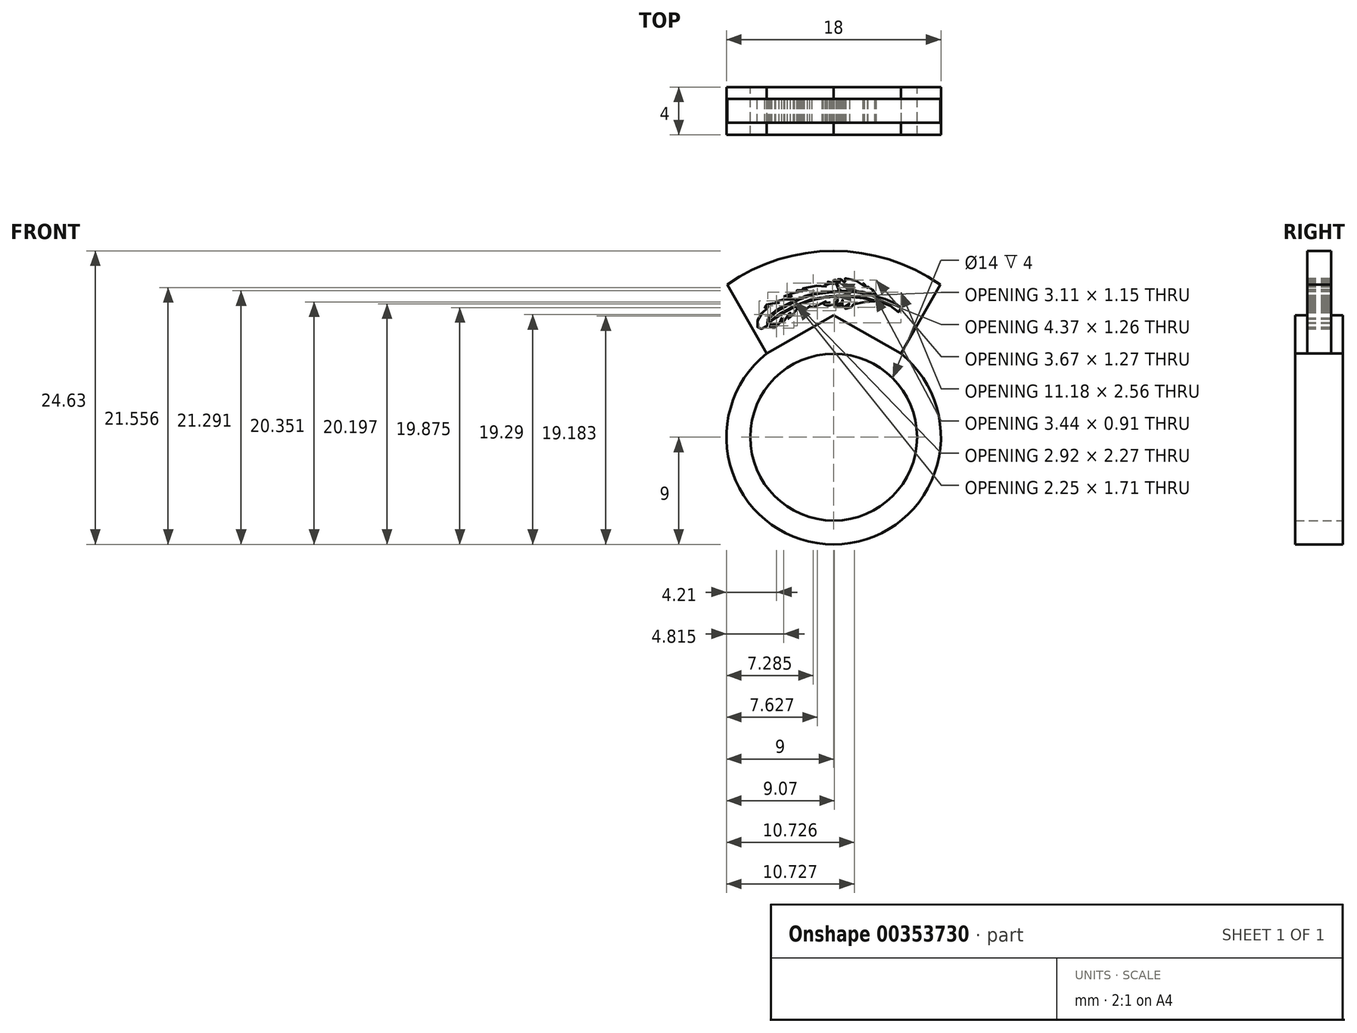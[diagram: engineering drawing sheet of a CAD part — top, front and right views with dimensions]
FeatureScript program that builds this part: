
annotation { "Feature Type Name" : "Feature", "Feature Type Description" : "" }
export const myFeature = defineFeature(function(context is Context, id is Id, definition is map)
    precondition{}
    {
        {
            var Q0;
            Q0=qCreatedBy(makeId("Front.planeOp"),FACE);
            var sketch = newSketch(context, id + "F0", { "sketchPlane" : qUnion([Q0])});
            skCircle(sketch, "E0", {"center": v(0, 0) * mm, "radius": 7 * mm});
            skCircle(sketch, "E1", {"center": v(0, 0) * mm, "radius": 9 * mm});
            skSolve(sketch);
        }
        {
            var Q0;
            Q0 = qSketchRegion(id + "F0", true);
            extrude(context, id + "F1", {"entities" : qUnion([Q0]), "depth" : 4 * mm});
        }
        {
            var Q0;
            Q0=makeQuery(id+"F1.opExtrude","CAP_FACE",FACE,{"disambiguationData":[OSD([sQuery(id+"F0.wireOp",EDGE,"E0"),sQuery(id+"F0.wireOp",EDGE,"E1")])],"isStart":false});
            var sketch = newSketch(context, id + "F2", { "sketchPlane" : qUnion([Q0])});
            skLineSegment(sketch, "E2", {"start": v(-5.64, 7.02) * mm, "end": v(-8.94, 12.8) * mm});
            skLineSegment(sketch, "E3", {"start": v(5.64, 7.02) * mm, "end": v(8.94, 12.8) * mm});
            skArc(sketch, "E4", {"start": v(8.94, 12.8) * mm, "mid": v(0, 15.63) * mm, "end": v(-8.94, 12.8) * mm});
            skSolve(sketch);
        }
        {
            var Q0;
            {var subQ0=sQuery(id+"F2.wireOp",EDGE,"E2");Q0=makeQuery(id+"F2.imprint","IMPRINT",FACE,{"disambiguationData":[TD([[makeQuery(id+"F2.imprint","IMPRINT",EDGE,{"derivedFrom":subQ0}),-1.0]])]});}
            extrude(context, id + "F3", {"entities" : qUnion([Q0]), "operationType" : NewBodyOperationType.ADD, "oppositeDirection" : true, "depth" : 4 * mm});
        }
        {
            var Q0;
            Q0=makeQuery(id+"F3.opExtrude","SWEPT_FACE",FACE,{"disambiguationData":[OSD([sQuery(id+"F2.wireOp",EDGE,"E2")])]});
            var sketch = newSketch(context, id + "F4", { "sketchPlane" : qUnion([Q0])});
            skLineSegment(sketch, "E5", {"start": v(1, 15.54) * mm, "end": v(1, 8.89) * mm});
            skLineSegment(sketch, "E6", {"start": v(1, 8.89) * mm, "end": v(3, 8.89) * mm});
            skLineSegment(sketch, "E7", {"start": v(3, 8.89) * mm, "end": v(3, 15.54) * mm});
            skLineSegment(sketch, "E8", {"start": v(3, 15.54) * mm, "end": v(1, 15.54) * mm});
            skSolve(sketch);
        }
        {
            var Q0;
            {var subQ0=sQuery(id+"F4.wireOp",EDGE,"E7");Q0=makeQuery(id+"F4.imprint","IMPRINT",FACE,{"disambiguationData":[TD([[makeQuery(id+"F4.imprint","IMPRINT",EDGE,{"derivedFrom":subQ0}),-1.0]])]});}
            var Q1;
            {var subQ0=sQuery(id+"F4.wireOp",EDGE,"E5");Q1=makeQuery(id+"F4.imprint","IMPRINT",FACE,{"disambiguationData":[TD([[makeQuery(id+"F4.imprint","IMPRINT",EDGE,{"derivedFrom":subQ0}),-1.0]])]});}
            extrude(context, id + "F5", {"entities" : qUnion([Q0, Q1]), "operationType" : NewBodyOperationType.REMOVE, "endBound" : BoundingType.THROUGH_ALL, "oppositeDirection" : true, "depth" : 25 * mm});
        }
        {
            var Q0;
            Q0=makeQuery(id+"F3.opExtrude","SWEPT_FACE",FACE,{"disambiguationData":[OSD([sQuery(id+"F2.wireOp",EDGE,"E3")])]});
            var sketch = newSketch(context, id + "F6", { "sketchPlane" : qUnion([Q0])});
            skLineSegment(sketch, "E9", {"start": v(-3, 15.54) * mm, "end": v(-3, 8.89) * mm});
            skLineSegment(sketch, "E10", {"start": v(-3, 8.89) * mm, "end": v(-1, 8.89) * mm});
            skLineSegment(sketch, "E11", {"start": v(-1, 8.89) * mm, "end": v(-1, 15.54) * mm});
            skLineSegment(sketch, "E12", {"start": v(-1, 15.54) * mm, "end": v(-3, 15.54) * mm});
            skSolve(sketch);
        }
        {
            var Q0;
            {var subQ0=sQuery(id+"F6.wireOp",EDGE,"E9");Q0=makeQuery(id+"F6.imprint","IMPRINT",FACE,{"disambiguationData":[TD([[makeQuery(id+"F6.imprint","IMPRINT",EDGE,{"derivedFrom":subQ0}),-1.0]])]});}
            var Q1;
            {var subQ0=sQuery(id+"F6.wireOp",EDGE,"E11");Q1=makeQuery(id+"F6.imprint","IMPRINT",FACE,{"disambiguationData":[TD([[makeQuery(id+"F6.imprint","IMPRINT",EDGE,{"derivedFrom":subQ0}),-1.0]])]});}
            extrude(context, id + "F7", {"entities" : qUnion([Q0, Q1]), "operationType" : NewBodyOperationType.REMOVE, "endBound" : BoundingType.THROUGH_ALL, "oppositeDirection" : true, "depth" : 25 * mm});
        }
        {
            var Q0;
            {var subQ0=sQuery(id+"F2.wireOp",EDGE,"E2");var subQ1=sQuery(id+"F2.wireOp",EDGE,"E4");var subQ2=makeQuery(id+"F3.opExtrude","SWEPT_EDGE",EDGE,{"disambiguationData":[OSD([subQ0,subQ1])]});Q0=makeQuery(id+"F5.boolean.opBoolean","COPY",FACE,{"derivedFrom":makeQuery(id+"F5.opExtrude","SWEPT_FACE",FACE,{"disambiguationData":[OSD([subQ0,subQ1]),TDD([makeQuery(id+"F4.imprint","IMPRINT",EDGE,{"disambiguationData":[TD([[makeQuery(id+"F4.imprint","INTERSECT",VERTEX,{"derivedFrom":[subQ2,makeQuery(id+"F3.opExtrude","CAP_EDGE",EDGE,{"disambiguationData":[OSD([subQ0])],"isStart":false})]}),-1.0]])],"derivedFrom":subQ2})])]})});}
            extrude(context, id + "F8", {"entities" : qUnion([Q0]), "operationType" : NewBodyOperationType.REMOVE, "endBound" : BoundingType.THROUGH_ALL, "oppositeDirection" : true, "depth" : 25 * mm});
        }
        {
            var Q0;
            {var subQ0=sQuery(id+"F2.wireOp",EDGE,"E2");var subQ1=sQuery(id+"F2.wireOp",EDGE,"E4");var subQ2=makeQuery(id+"F3.opExtrude","SWEPT_EDGE",EDGE,{"disambiguationData":[OSD([subQ0,subQ1])]});Q0=makeQuery(id+"F5.boolean.opBoolean","COPY",FACE,{"derivedFrom":makeQuery(id+"F5.opExtrude","SWEPT_FACE",FACE,{"disambiguationData":[OSD([subQ0,subQ1]),TDD([makeQuery(id+"F4.imprint","IMPRINT",EDGE,{"disambiguationData":[TD([[makeQuery(id+"F4.imprint","INTERSECT",VERTEX,{"derivedFrom":[subQ2,makeQuery(id+"F3.opExtrude","CAP_EDGE",EDGE,{"disambiguationData":[OSD([subQ0])],"isStart":true})]}),1.0]])],"derivedFrom":subQ2})])]})});}
            extrude(context, id + "F9", {"entities" : qUnion([Q0]), "operationType" : NewBodyOperationType.REMOVE, "endBound" : BoundingType.THROUGH_ALL, "oppositeDirection" : true, "depth" : 25 * mm});
        }
        {
            var Q0;
            {var subQ0=sQuery(id+"F2.wireOp",EDGE,"E3");var subQ1=sQuery(id+"F2.wireOp",EDGE,"E4");var subQ2=makeQuery(id+"F3.opExtrude","SWEPT_EDGE",EDGE,{"disambiguationData":[OSD([subQ0,subQ1])]});Q0=makeQuery(id+"F7.boolean.opBoolean","COPY",FACE,{"derivedFrom":makeQuery(id+"F7.opExtrude","SWEPT_FACE",FACE,{"disambiguationData":[OSD([subQ0,subQ1]),TDD([makeQuery(id+"F6.imprint","IMPRINT",EDGE,{"disambiguationData":[TD([[makeQuery(id+"F6.imprint","INTERSECT",VERTEX,{"derivedFrom":[subQ2,makeQuery(id+"F3.opExtrude","CAP_EDGE",EDGE,{"disambiguationData":[OSD([subQ0])],"isStart":true})]}),1.0]])],"derivedFrom":subQ2})])]})});}
            var Q1;
            {var subQ0=sQuery(id+"F2.wireOp",EDGE,"E3");var subQ1=sQuery(id+"F2.wireOp",EDGE,"E4");var subQ2=makeQuery(id+"F3.opExtrude","SWEPT_EDGE",EDGE,{"disambiguationData":[OSD([subQ0,subQ1])]});Q1=makeQuery(id+"F7.boolean.opBoolean","COPY",FACE,{"derivedFrom":makeQuery(id+"F7.opExtrude","SWEPT_FACE",FACE,{"disambiguationData":[OSD([subQ0,subQ1]),TDD([makeQuery(id+"F6.imprint","IMPRINT",EDGE,{"disambiguationData":[TD([[makeQuery(id+"F6.imprint","INTERSECT",VERTEX,{"derivedFrom":[subQ2,makeQuery(id+"F3.opExtrude","CAP_EDGE",EDGE,{"disambiguationData":[OSD([subQ0])],"isStart":false})]}),-1.0]])],"derivedFrom":subQ2})])]})});}
            extrude(context, id + "F10", {"entities" : qUnion([Q0, Q1]), "operationType" : NewBodyOperationType.REMOVE, "endBound" : BoundingType.THROUGH_ALL, "oppositeDirection" : true, "depth" : 25 * mm});
        }
        {
            var Q0;
            {var subQ0=sQuery(id+"F6.wireOp",EDGE,"E11");var subQ1=sQuery(id+"F2.wireOp",EDGE,"E4");var subQ2=sQuery(id+"F4.wireOp",EDGE,"E5");Q0=makeQuery(id+"F10.boolean.opBoolean","MERGE",FACE,{"derivedFrom":[makeQuery(id+"F8.boolean.opBoolean","MERGE",FACE,{"derivedFrom":[makeQuery(id+"F7.boolean.opBoolean","MERGE",FACE,{"derivedFrom":[makeQuery(id+"F5.boolean.opBoolean","COPY",FACE,{"derivedFrom":makeQuery(id+"F5.opExtrude","SWEPT_FACE",FACE,{"disambiguationData":[OSD([subQ2])]})}),makeQuery(id+"F7.opExtrude","SWEPT_FACE",FACE,{"disambiguationData":[OSD([subQ0])]})]}),makeQuery(id+"F8.opExtrude","SWEPT_FACE",FACE,{"disambiguationData":[OSD([sQuery(id+"F2.wireOp",EDGE,"E2"),subQ1,subQ2,sQuery(id+"F4.wireOp",EDGE,"E8")])]})]}),makeQuery(id+"F10.opExtrude","SWEPT_FACE",FACE,{"disambiguationData":[OSD([sQuery(id+"F2.wireOp",EDGE,"E3"),subQ1,subQ0,sQuery(id+"F6.wireOp",EDGE,"E12")])]})]});}
            var sketch = newSketch(context, id + "F11", { "sketchPlane" : qUnion([Q0])});
            skFitSpline(sketch, "E13", {"points": [v(-5.66, 10.87) * mm, v(-5.57, 10.45) * mm, v(-5.18, 10.74) * mm, v(-4.16, 11.27) * mm, v(-2.41, 11.75) * mm, v(-0.52, 11.88) * mm, v(0, 11.85) * mm, v(1.4, 11.68) * mm, v(3.3, 11) * mm, v(5.28, 9.8) * mm, v(5.51, 9.57) * mm, v(5.41, 9.99) * mm, v(4.45, 10.75) * mm, v(3.34, 11.32) * mm, v(1.84, 11.93) * mm, v(0, 12.17) * mm, v(-1.23, 12.22) * mm, v(-2.88, 12) * mm, v(-4.84, 11.4) * mm, v(-5.38, 11.12) * mm, v(-5.66, 10.87) * mm]});
            skSolve(sketch);
        }
        {
            var Q0;
            Q0 = qSketchRegion(id + "F11", true);
            extrude(context, id + "F12", {"entities" : qUnion([Q0]), "operationType" : NewBodyOperationType.REMOVE, "endBound" : BoundingType.THROUGH_ALL, "oppositeDirection" : true, "depth" : 25 * mm});
        }
        {
            var Q0;
            {var subQ0=sQuery(id+"F6.wireOp",EDGE,"E11");var subQ1=sQuery(id+"F2.wireOp",EDGE,"E4");var subQ2=sQuery(id+"F4.wireOp",EDGE,"E5");Q0=makeQuery(id+"F10.boolean.opBoolean","MERGE",FACE,{"derivedFrom":[makeQuery(id+"F8.boolean.opBoolean","MERGE",FACE,{"derivedFrom":[makeQuery(id+"F7.boolean.opBoolean","MERGE",FACE,{"derivedFrom":[makeQuery(id+"F5.boolean.opBoolean","COPY",FACE,{"derivedFrom":makeQuery(id+"F5.opExtrude","SWEPT_FACE",FACE,{"disambiguationData":[OSD([subQ2])]})}),makeQuery(id+"F7.opExtrude","SWEPT_FACE",FACE,{"disambiguationData":[OSD([subQ0])]})]}),makeQuery(id+"F8.opExtrude","SWEPT_FACE",FACE,{"disambiguationData":[OSD([sQuery(id+"F2.wireOp",EDGE,"E2"),subQ1,subQ2,sQuery(id+"F4.wireOp",EDGE,"E8")])]})]}),makeQuery(id+"F10.opExtrude","SWEPT_FACE",FACE,{"disambiguationData":[OSD([sQuery(id+"F2.wireOp",EDGE,"E3"),subQ1,subQ0,sQuery(id+"F6.wireOp",EDGE,"E12")])]})]});}
            var sketch = newSketch(context, id + "F13", { "sketchPlane" : qUnion([Q0])});
            skFitSpline(sketch, "E14", {"points": [v(-3.45, 11.42) * mm, v(-3.13, 11.52) * mm, v(-2.56, 11.65) * mm, v(-1.78, 11.74) * mm, v(-0.99, 11.78) * mm, v(-0.56, 11.8) * mm, v(-0.22, 11.77) * mm, v(-0.31, 11.58) * mm, v(-0.26, 11.2) * mm, v(0, 10.91) * mm, v(-0.19, 10.94) * mm, v(-0.51, 11.24) * mm, v(-0.4, 11.02) * mm, v(-0.28, 10.9) * mm, v(-0.43, 10.93) * mm, v(-0.57, 11.08) * mm, v(-0.7, 11.33) * mm, v(-0.75, 11.52) * mm, v(-0.78, 11.17) * mm, v(-0.65, 10.91) * mm, v(-1.1, 11.03) * mm, v(-1.35, 11.24) * mm, v(-1.28, 11.06) * mm, v(-0.95, 10.78) * mm, v(-1.27, 10.85) * mm, v(-1.58, 11) * mm, v(-1.73, 11.18) * mm, v(-3.45, 11.42) * mm]});
            skFitSpline(sketch, "E15", {"points": [v(-3.56, 11.92) * mm, v(-2.94, 12.08) * mm, v(-2.33, 12.2) * mm, v(-1.6, 12.27) * mm, v(-0.95, 12.3) * mm, v(-0.5, 12.3) * mm, v(-0.35, 12.58) * mm, v(-0.32, 12.88) * mm, v(-0.14, 13.12) * mm, v(0.14, 13.18) * mm, v(-0.17, 13.2) * mm, v(-0.39, 13.04) * mm, v(-0.48, 12.86) * mm, v(-0.54, 13) * mm, v(-0.5, 13.16) * mm, v(-0.32, 13.28) * mm, v(-0.64, 13.24) * mm, v(-0.86, 13.08) * mm, v(-0.93, 12.96) * mm, v(-1.03, 13.08) * mm, v(-0.82, 13.3) * mm, v(-1.92, 13.11) * mm, v(-2.6, 12.69) * mm, v(-2.48, 12.9) * mm, v(-2.77, 12.65) * mm, v(-2.89, 12.42) * mm, v(-2.88, 12.69) * mm, v(-3.5, 12.05) * mm, v(-3.56, 11.92) * mm]});
            skSolve(sketch);
        }
        {
            var Q0;
            Q0=makeQuery(id+"F13.imprint","IMPRINT",FACE,{"disambiguationData":[TD([[makeQuery(id+"F13.imprint","IMPRINT",EDGE,{"derivedFrom":sQuery(id+"F13.wireOp",EDGE,"E14")}),-1.0]])]});
            var Q1;
            Q1=makeQuery(id+"F13.imprint","IMPRINT",FACE,{"disambiguationData":[TD([[makeQuery(id+"F13.imprint","IMPRINT",EDGE,{"derivedFrom":sQuery(id+"F13.wireOp",EDGE,"c0ec5056-5226-495e-9444-eb4ab02b29c7")}),1.0]])]});
            extrude(context, id + "F14", {"entities" : qUnion([Q0, Q1]), "operationType" : NewBodyOperationType.REMOVE, "endBound" : BoundingType.THROUGH_ALL, "oppositeDirection" : true, "depth" : 25 * mm});
        }
        {
            var Q0;
            {var subQ0=sQuery(id+"F6.wireOp",EDGE,"E11");var subQ1=sQuery(id+"F2.wireOp",EDGE,"E4");var subQ2=sQuery(id+"F4.wireOp",EDGE,"E5");Q0=makeQuery(id+"F10.boolean.opBoolean","MERGE",FACE,{"derivedFrom":[makeQuery(id+"F8.boolean.opBoolean","MERGE",FACE,{"derivedFrom":[makeQuery(id+"F7.boolean.opBoolean","MERGE",FACE,{"derivedFrom":[makeQuery(id+"F5.boolean.opBoolean","COPY",FACE,{"derivedFrom":makeQuery(id+"F5.opExtrude","SWEPT_FACE",FACE,{"disambiguationData":[OSD([subQ2])]})}),makeQuery(id+"F7.opExtrude","SWEPT_FACE",FACE,{"disambiguationData":[OSD([subQ0])]})]}),makeQuery(id+"F8.opExtrude","SWEPT_FACE",FACE,{"disambiguationData":[OSD([sQuery(id+"F2.wireOp",EDGE,"E2"),subQ1,subQ2,sQuery(id+"F4.wireOp",EDGE,"E8")])]})]}),makeQuery(id+"F10.opExtrude","SWEPT_FACE",FACE,{"disambiguationData":[OSD([sQuery(id+"F2.wireOp",EDGE,"E3"),subQ1,subQ0,sQuery(id+"F6.wireOp",EDGE,"E12")])]})]});}
            var sketch = newSketch(context, id + "F15", { "sketchPlane" : qUnion([Q0])});
            skSolve(sketch);
        }
        {
            var Q0;
            Q0 = qSketchRegion(id + "F13", true);
            var Q1;
            Q1=makeQuery(id+"F15.imprint","IMPRINT",FACE,{"disambiguationData":[TD([[makeQuery(id+"F15.imprint","IMPRINT",EDGE,{"derivedFrom":makeQuery(id+"F14.boolean.opBoolean","COPY",EDGE,{"derivedFrom":makeQuery(id+"F14.opExtrude","CAP_EDGE",EDGE,{"disambiguationData":[OSD([sQuery(id+"F13.wireOp",EDGE,"E14")])],"isStart":true})})}),-1.0]])]});
            extrude(context, id + "F16", {"entities" : qUnion([Q0, Q1]), "operationType" : NewBodyOperationType.REMOVE, "endBound" : BoundingType.THROUGH_ALL, "oppositeDirection" : true, "depth" : 25 * mm});
        }
        {
            var Q0;
            {var subQ0=sQuery(id+"F6.wireOp",EDGE,"E11");var subQ1=sQuery(id+"F2.wireOp",EDGE,"E4");var subQ2=sQuery(id+"F4.wireOp",EDGE,"E5");Q0=makeQuery(id+"F10.boolean.opBoolean","MERGE",FACE,{"derivedFrom":[makeQuery(id+"F8.boolean.opBoolean","MERGE",FACE,{"derivedFrom":[makeQuery(id+"F7.boolean.opBoolean","MERGE",FACE,{"derivedFrom":[makeQuery(id+"F5.boolean.opBoolean","COPY",FACE,{"derivedFrom":makeQuery(id+"F5.opExtrude","SWEPT_FACE",FACE,{"disambiguationData":[OSD([subQ2])]})}),makeQuery(id+"F7.opExtrude","SWEPT_FACE",FACE,{"disambiguationData":[OSD([subQ0])]})]}),makeQuery(id+"F8.opExtrude","SWEPT_FACE",FACE,{"disambiguationData":[OSD([sQuery(id+"F2.wireOp",EDGE,"E2"),subQ1,subQ2,sQuery(id+"F4.wireOp",EDGE,"E8")])]})]}),makeQuery(id+"F10.opExtrude","SWEPT_FACE",FACE,{"disambiguationData":[OSD([sQuery(id+"F2.wireOp",EDGE,"E3"),subQ1,subQ0,sQuery(id+"F6.wireOp",EDGE,"E12")])]})]});}
            var sketch = newSketch(context, id + "F17", { "sketchPlane" : qUnion([Q0])});
            skFitSpline(sketch, "E16", {"points": [v(-0.47, 12.28) * mm, v(-0.22, 12.27) * mm, v(-0.04, 12.26) * mm, v(0.27, 12.23) * mm, v(0.71, 12.2) * mm, v(1.2, 12.13) * mm, v(1.55, 12.07) * mm, v(2.1, 11.95) * mm, v(2.6, 11.77) * mm, v(3.2, 11.46) * mm, v(3.36, 11.55) * mm, v(3.73, 11.66) * mm, v(4.1, 11.61) * mm, v(3.87, 11.73) * mm, v(3.64, 11.77) * mm, v(3.37, 11.76) * mm, v(3.6, 11.86) * mm, v(3.83, 11.87) * mm, v(4.17, 11.81) * mm, v(4.06, 11.88) * mm, v(3.33, 12.1) * mm, v(2.8, 12.14) * mm, v(3.12, 12.24) * mm, v(3.28, 12.23) * mm, v(3.13, 12.3) * mm, v(2.53, 12.38) * mm, v(2.21, 12.33) * mm, v(2.54, 12.45) * mm, v(2.62, 12.46) * mm, v(2.1, 12.62) * mm, v(0.93, 12.7) * mm, v(0.64, 12.62) * mm, v(0.78, 12.72) * mm, v(0.95, 12.77) * mm, v(0.71, 12.77) * mm, v(0.36, 12.66) * mm, v(0.52, 12.8) * mm, v(0.71, 12.86) * mm, v(0.53, 12.91) * mm, v(0.1, 12.84) * mm, v(-0.07, 12.73) * mm, v(0.07, 12.91) * mm, v(0.32, 13.03) * mm, v(0.51, 13.05) * mm, v(0.18, 13.1) * mm, v(-0.22, 12.84) * mm, v(-0.32, 12.4) * mm, v(-0.47, 12.28) * mm]});
            skFitSpline(sketch, "E17", {"points": [v(-0.18, 11.77) * mm, v(0, 11.77) * mm, v(0.24, 11.75) * mm, v(0.58, 11.71) * mm, v(0.93, 11.68) * mm, v(1.28, 11.61) * mm, v(1.75, 11.52) * mm, v(2.22, 11.37) * mm, v(2.65, 11.22) * mm, v(3, 11.08) * mm, v(2.93, 10.97) * mm, v(2.95, 10.75) * mm, v(3.08, 10.65) * mm, v(2.9, 10.68) * mm, v(2.8, 10.83) * mm, v(2.79, 10.9) * mm, v(2.75, 10.84) * mm, v(2.8, 10.68) * mm, v(2.84, 10.62) * mm, v(2.7, 10.7) * mm, v(2.61, 10.84) * mm, v(2.6, 10.92) * mm, v(2.47, 10.84) * mm, v(2.53, 10.66) * mm, v(2.34, 10.72) * mm, v(2.3, 10.75) * mm, v(2.15, 10.87) * mm, v(1.82, 11.13) * mm, v(1.89, 11) * mm, v(2, 10.91) * mm, v(1.81, 10.94) * mm, v(1.2, 11.1) * mm, v(0.58, 11.43) * mm, v(0.7, 11.29) * mm, v(0.88, 11.2) * mm, v(0.78, 11.19) * mm, v(0.57, 11.23) * mm, v(0.22, 11.46) * mm, v(0.3, 11.37) * mm, v(0.43, 11.24) * mm, v(0.63, 11.14) * mm, v(0.86, 11.09) * mm, v(0.66, 11.05) * mm, v(0.35, 11.03) * mm, v(0.07, 11.1) * mm, v(-0.09, 11.21) * mm, v(-0.15, 11.27) * mm, v(-0.22, 11.37) * mm, v(-0.26, 11.48) * mm, v(-0.24, 11.6) * mm, v(-0.18, 11.77) * mm]});
            skSolve(sketch);
        }
        {
            var Q0;
            Q0 = qSketchRegion(id + "F17", true);
            extrude(context, id + "F18", {"entities" : qUnion([Q0]), "operationType" : NewBodyOperationType.REMOVE, "endBound" : BoundingType.THROUGH_ALL, "oppositeDirection" : true, "depth" : 25 * mm});
        }
        {
            var Q0;
            {var subQ0=sQuery(id+"F6.wireOp",EDGE,"E11");var subQ1=sQuery(id+"F2.wireOp",EDGE,"E4");var subQ2=sQuery(id+"F4.wireOp",EDGE,"E5");Q0=makeQuery(id+"F10.boolean.opBoolean","MERGE",FACE,{"derivedFrom":[makeQuery(id+"F8.boolean.opBoolean","MERGE",FACE,{"derivedFrom":[makeQuery(id+"F7.boolean.opBoolean","MERGE",FACE,{"derivedFrom":[makeQuery(id+"F5.boolean.opBoolean","COPY",FACE,{"derivedFrom":makeQuery(id+"F5.opExtrude","SWEPT_FACE",FACE,{"disambiguationData":[OSD([subQ2])]})}),makeQuery(id+"F7.opExtrude","SWEPT_FACE",FACE,{"disambiguationData":[OSD([subQ0])]})]}),makeQuery(id+"F8.opExtrude","SWEPT_FACE",FACE,{"disambiguationData":[OSD([sQuery(id+"F2.wireOp",EDGE,"E2"),subQ1,subQ2,sQuery(id+"F4.wireOp",EDGE,"E8")])]})]}),makeQuery(id+"F10.opExtrude","SWEPT_FACE",FACE,{"disambiguationData":[OSD([sQuery(id+"F2.wireOp",EDGE,"E3"),subQ1,subQ0,sQuery(id+"F6.wireOp",EDGE,"E12")])]})]});}
            var sketch = newSketch(context, id + "F19", { "sketchPlane" : qUnion([Q0])});
            skFitSpline(sketch, "E18", {"points": [v(3.33, 11.42) * mm, v(3.6, 11.3) * mm, v(4.06, 11.07) * mm, v(4.6, 10.76) * mm, v(5.12, 10.44) * mm, v(5.44, 10.08) * mm, v(5.6, 9.58) * mm, v(5.48, 9.49) * mm, v(5.8, 9.2) * mm, v(6.3, 9.11) * mm, v(6.41, 9.69) * mm, v(5.78, 10.67) * mm, v(5.41, 10.95) * mm, v(5.62, 10.95) * mm, v(5.79, 10.9) * mm, v(5.69, 11.06) * mm, v(5.28, 11.2) * mm, v(4.58, 11.28) * mm, v(4.82, 11.34) * mm, v(4.94, 11.34) * mm, v(4.61, 11.44) * mm, v(3.75, 11.57) * mm, v(3.33, 11.42) * mm]});
            skFitSpline(sketch, "E19", {"points": [v(3.06, 11.04) * mm, v(3.42, 10.85) * mm, v(3.98, 10.57) * mm, v(4.86, 10.03) * mm, v(5.35, 9.6) * mm, v(5.28, 9.47) * mm, v(5.37, 9.27) * mm, v(5.18, 9.32) * mm, v(4.88, 9.57) * mm, v(5.04, 9.25) * mm, v(5.18, 9.18) * mm, v(4.87, 9.2) * mm, v(4.4, 9.84) * mm, v(4.36, 10) * mm, v(4.34, 9.62) * mm, v(3.8, 10.28) * mm, v(3.64, 10.51) * mm, v(3.74, 10.09) * mm, v(3.9, 9.91) * mm, v(3.63, 10.04) * mm, v(3.29, 10.46) * mm, v(3.17, 10.65) * mm, v(3.05, 10.77) * mm, v(3.06, 11.04) * mm]});
            skSolve(sketch);
        }
        {
            var Q0;
            Q0 = qSketchRegion(id + "F19", true);
            extrude(context, id + "F20", {"entities" : qUnion([Q0]), "operationType" : NewBodyOperationType.REMOVE, "endBound" : BoundingType.THROUGH_ALL, "oppositeDirection" : true, "depth" : 25 * mm});
        }
    });
